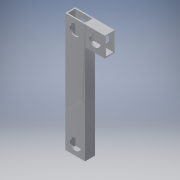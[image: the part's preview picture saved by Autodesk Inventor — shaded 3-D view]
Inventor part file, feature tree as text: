
AUTODESK INVENTOR PART (.ipt)
format: ipt  version: 2016 (Build 200138000, 138)  size: 153,088 bytes
history: native  units: in
note: dims shown in document units (in); Inventor stores cm internally (conversion verified against a paired STEP export)
features: extrude x5, sketch x5
ambient origin geometry x8: Origin, YZ Plane, XZ Plane, XY Plane, X Axis, Y Axis, Z Axis, Center Point
bodies: Solid1 (feature_tree)
feature tree (10):
  extrude  "Extrusion1"  Depth=1.0in
  extrude  "Extrusion2"  Depth=0.1253in
  extrude  "Extrusion3"  Depth=0.125in
  extrude  "Extrusion4"  Depth=2.0in
  extrude  "Extrusion5"  Depth=0.125in
  sketch  "Sketch1"  dims[d0=2.0in d1=1.0in]
  sketch  "Sketch2"  dims[d2=0.125in d3=0.1253in]
  sketch  "Sketch3"  dims[d4=0.125in d5=0.125in]
  sketch  "Sketch4"  dims[d6=12.0in d7=0.0in d8=2.0in]
  sketch  "Sketch5"  dims[d9=0.125in d10=0.125in d11=2.0in d12=0.0in d13=1.0in d14=1.125in d15=2.0in d16=0.0in d17=1.0in d18=1.125in d19=2.0in d20=0.0in d21=1.0in d22=1.125in d23=1.0in d24=1.0in d25=0.0in]
